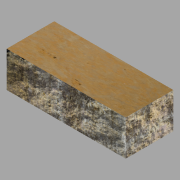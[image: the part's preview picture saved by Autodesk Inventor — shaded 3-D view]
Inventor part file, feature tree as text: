
AUTODESK INVENTOR PART (.ipt)
format: ipt  version: 2022.2 (Build 262287000, 287)  size: 135,680 bytes
history: native  units: in
note: dims shown in document units (in); Inventor stores cm internally (conversion verified against a paired STEP export)
features: extrude x1, sketch x1
ambient origin geometry x8: Origin, YZ Plane, XZ Plane, XY Plane, X Axis, Y Axis, Z Axis, Center Point
bodies: Solid1 (feature_tree)
feature tree (2):
  extrude  "Extrusion1"  Depth=24.0in
  sketch  "Sketch1"  dims[d0=18.0in d1=24.0in d2=60.0in d3=0.0in]
